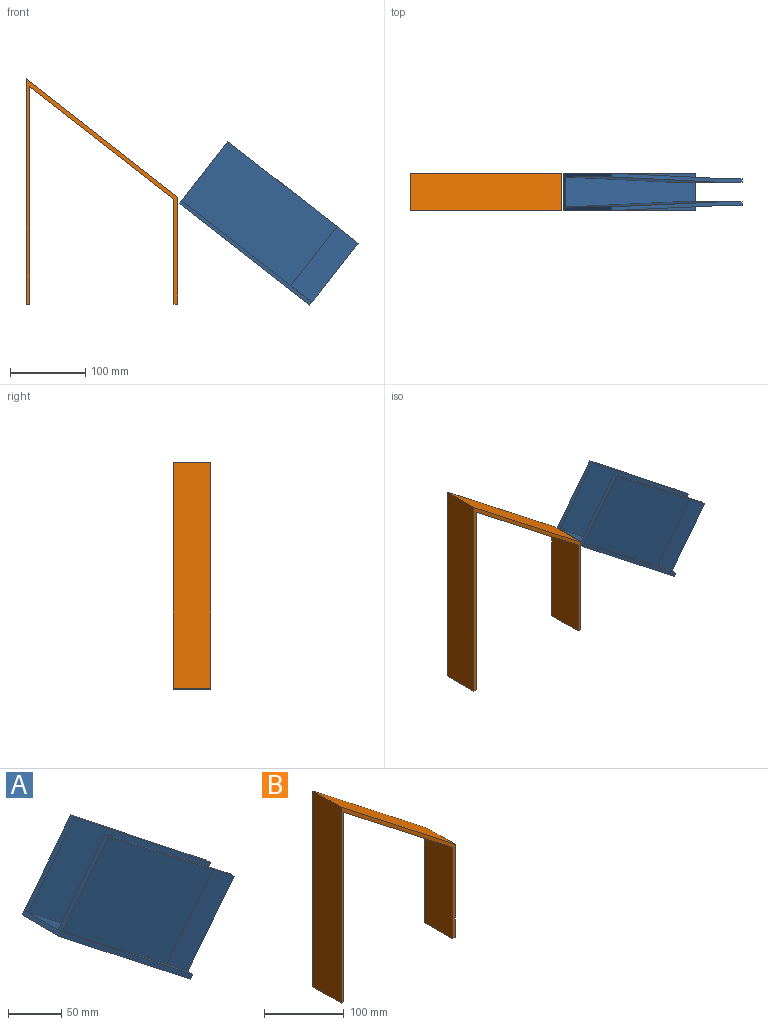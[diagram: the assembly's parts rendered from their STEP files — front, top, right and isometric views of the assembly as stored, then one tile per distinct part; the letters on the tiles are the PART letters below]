
ASSEMBLY  parts=2 mates=1
PART A: 20 faces, bbox 238.3x50x218.3 mm
  f0: plane 173.5x135.55mm, normal (0.62,0,0.79), area 894.3mm2, adj f5,f6,f17,f18
  f1: plane 173.5x135.55mm, normal (0.62,0,0.79), area 894.3mm2, adj f5,f7,f10,f11
  f2: plane 173.5x135.55mm, normal (0.62,0,0.79), area 7018.8mm2, adj f3,f5,f8,f9,f12,f14,f15,f16
  f3: plane 50x3.8mm, normal (-0.76,0,0.65), area 250.2mm2, adj f2,f4,f6,f7
  f4: plane 173.68x135.69mm, normal (-0.62,0,-0.79), area 11019.8mm2, adj f3,f5,f6,f7
  f5: plane 82.74x64.64mm, normal (0.79,0,-0.62), area 1250mm2, adj f0,f1,f2,f4,f6,f7,f9,f10
  f6: plane 176.76x139.49mm, normal (0,-1,0), area 1101.4mm2, adj f0,f3,f4,f5
  f7: plane 176.76x139.49mm, normal (0,1,0), area 1101.4mm2, adj f1,f3,f4,f5
  f8: plane 207.17x192.56mm, normal (-0.03,-1,0.02), area 18490.9mm2, adj f2,f9,f12,f13
  f9: plane 100.56x89.41mm, normal (0,-1,0), area 3533.4mm2, adj f2,f5,f8,f13
  f10: plane 100.56x89.41mm, normal (0,1,0), area 3533.4mm2, adj f1,f5,f11,f13
  f11: plane 207.22x192.6mm, normal (0.03,1,-0.02), area 18497.4mm2, adj f1,f10,f12,f13
  f12: plane 78.84x61.62mm, normal (-0.79,-0.01,0.62), area 500.3mm2, adj f2,f8,f11,f13
  f13: plane 173.5x135.55mm, normal (0.62,0,0.79), area 1100.7mm2, adj f5,f8,f9,f10,f11,f12
  f14: plane 100.56x89.41mm, normal (0,1,0), area 3533.4mm2, adj f2,f5,f15,f19
  f15: plane 207.17x192.56mm, normal (-0.03,1,0.02), area 18490.9mm2, adj f2,f14,f16,f19
  f16: plane 78.84x61.62mm, normal (-0.79,0.01,0.62), area 500.3mm2, adj f2,f15,f17,f19
  f17: plane 207.22x192.6mm, normal (0.03,-1,-0.02), area 18497.4mm2, adj f0,f16,f18,f19
  f18: plane 100.56x89.41mm, normal (0,-1,0), area 3533.4mm2, adj f0,f5,f17,f19
  f19: plane 173.5x135.55mm, normal (0.62,0,0.79), area 1100.7mm2, adj f5,f14,f15,f16,f17,f18
PART B: 10 faces, bbox 202x50x300.3 mm
  f0: plane 50x5mm, normal (0,0,-1), area 250mm2, adj f1,f7,f8,f9
  f1: plane 290x50mm, normal (1,0,0), area 14500mm2, adj f0,f2,f8,f9
  f2: plane 192x150mm, normal (-0.62,0,-0.79), area 12182.4mm2, adj f1,f3,f8,f9
  f3: plane 140x50mm, normal (-1,0,0), area 7000mm2, adj f2,f4,f8,f9
  f4: plane 50x5mm, normal (0,0,-1), area 250mm2, adj f3,f5,f8,f9
  f5: plane 142.44x50mm, normal (1,0,0), area 7121.9mm2, adj f4,f6,f8,f9
  f6: plane 202x157.81mm, normal (0.62,0,0.79), area 12816.9mm2, adj f5,f7,f8,f9
  f7: plane 300.25x50mm, normal (-1,0,0), area 15012.6mm2, adj f0,f6,f8,f9
  f8: plane 300.25x202mm, normal (0,-1,0), area 3431.7mm2, adj f0,f1,f2,f3,f4,f5,f6,f7
  f9: plane 300.25x202mm, normal (0,1,0), area 3431.7mm2, adj f0,f1,f2,f3,f4,f5,f6,f7
PLACE A t=(192.85,0,96.9)mm
PLACE B t=(3.41,0,4.37)mm
MATE planar A.f2 <-> B.f6  axis (0.62,0,0.79) through (151.55,-25,142.44)mm
